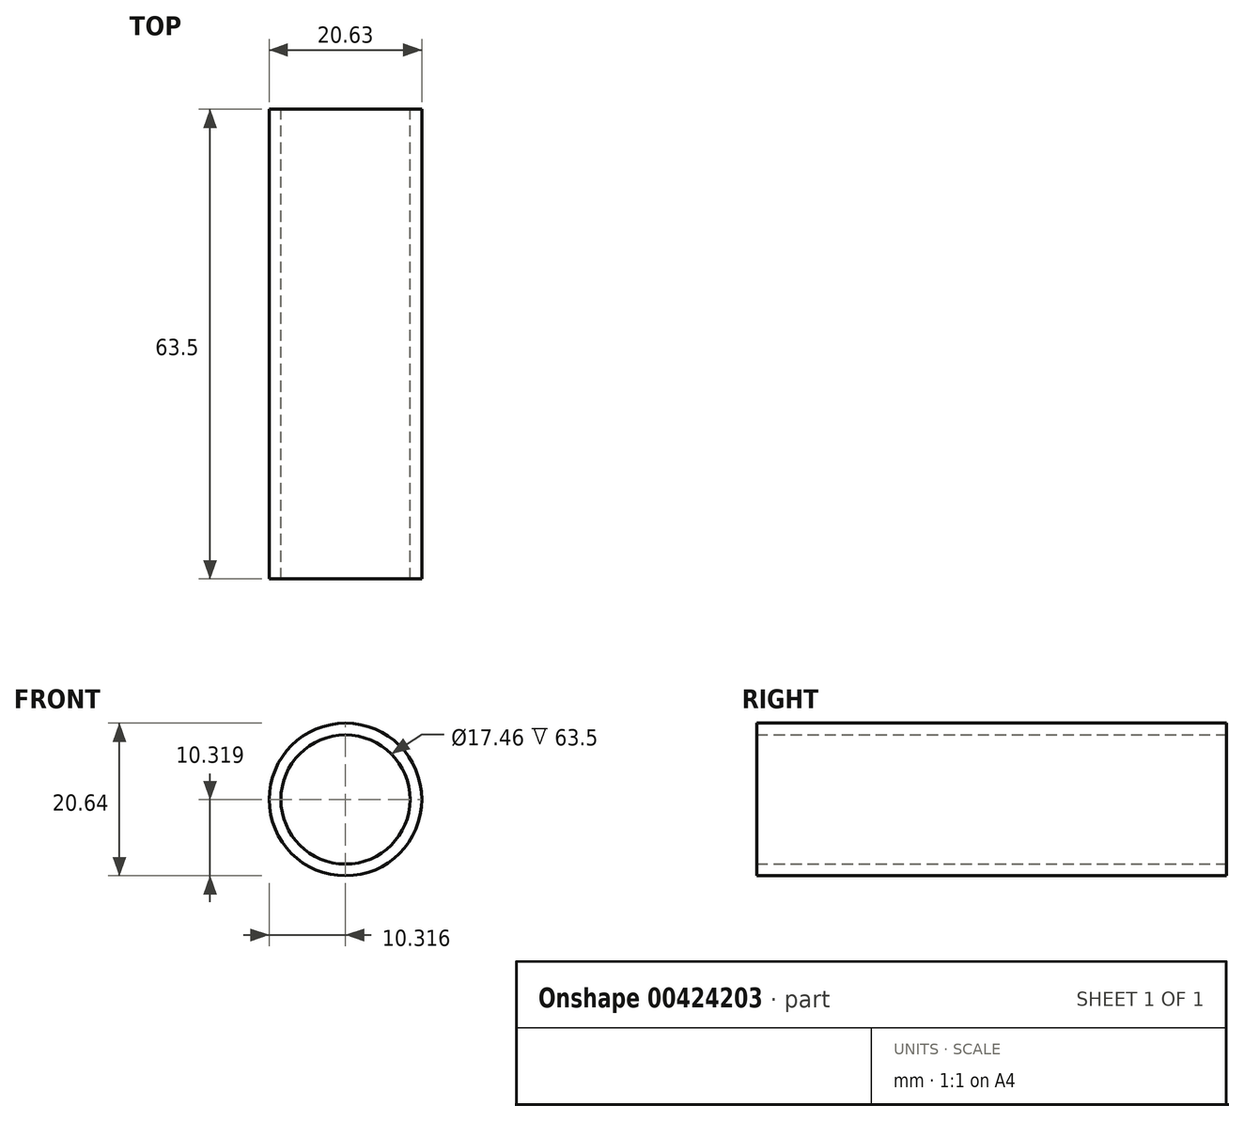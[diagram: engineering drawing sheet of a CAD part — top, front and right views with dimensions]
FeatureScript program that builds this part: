
annotation { "Feature Type Name" : "Feature", "Feature Type Description" : "" }
export const myFeature = defineFeature(function(context is Context, id is Id, definition is map)
    precondition{}
    {
        {
            var Q0;
            Q0=qCreatedBy(makeId("Front.planeOp"),FACE);
            var sketch = newSketch(context, id + "F0", { "sketchPlane" : qUnion([Q0])});
            skCircle(sketch, "E0", {"center": v(0.78, 0.26) * mm, "radius": 10.32 * mm});
            skCircle(sketch, "E1", {"center": v(0.78, 0.26) * mm, "radius": 8.73 * mm});
            skSolve(sketch);
        }
        {
            var Q0;
            Q0=makeQuery(id+"F0.imprint","IMPRINT",FACE,{"disambiguationData":[TD([[makeQuery(id+"F0.imprint","IMPRINT",EDGE,{"derivedFrom":sQuery(id+"F0.wireOp",EDGE,"E0")}),1.0]])]});
            extrude(context, id + "F1", {"entities" : qUnion([Q0]), "depth" : 63.5 * mm});
        }
    });
